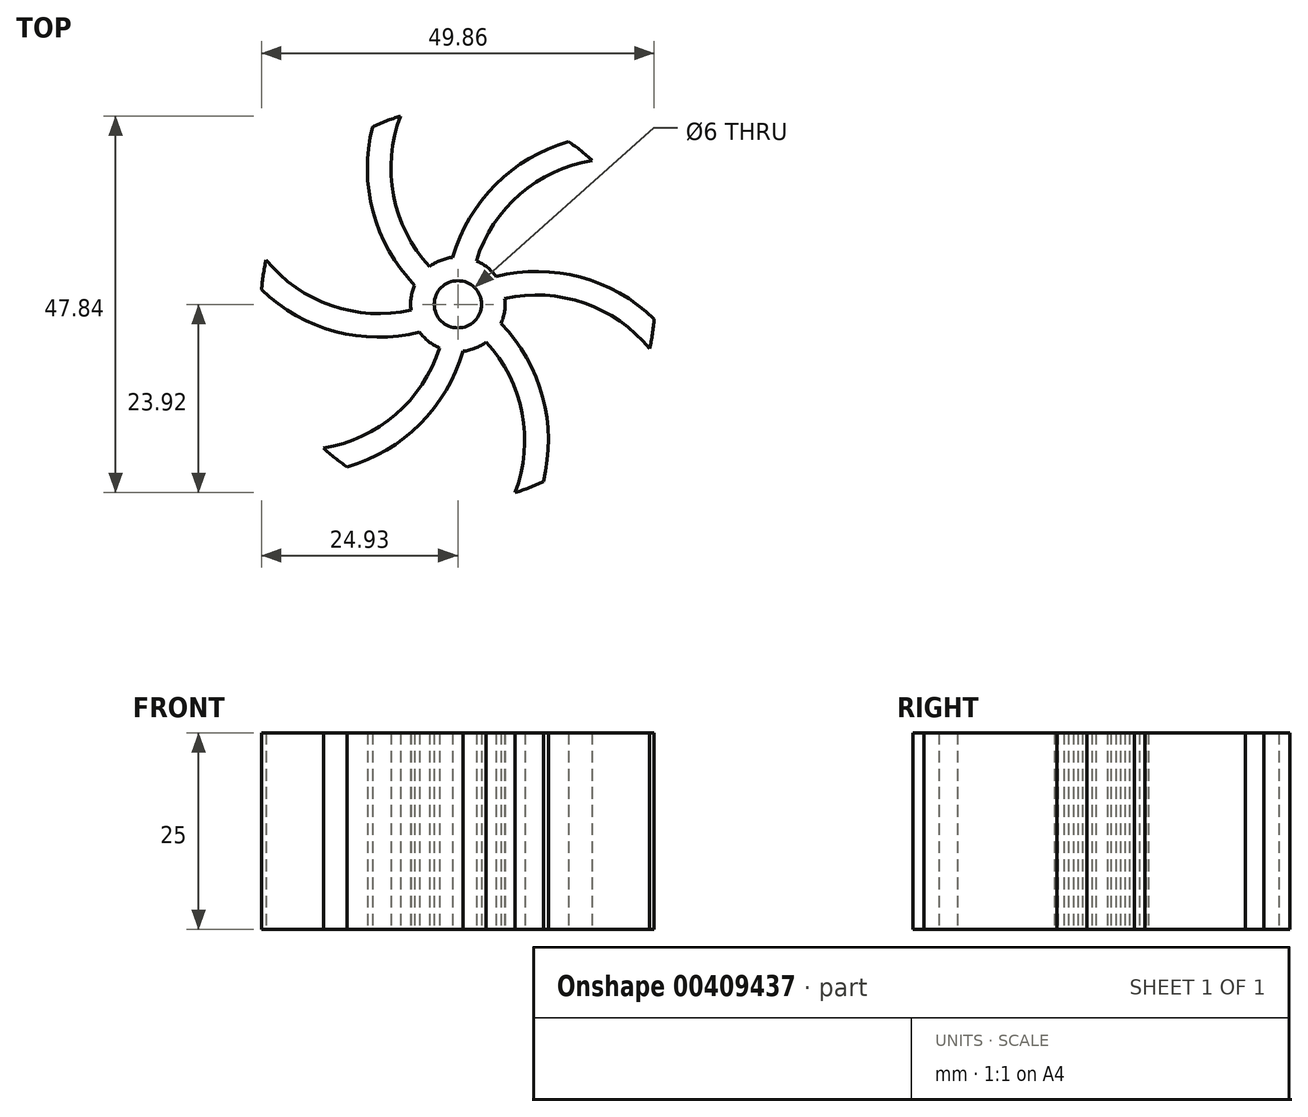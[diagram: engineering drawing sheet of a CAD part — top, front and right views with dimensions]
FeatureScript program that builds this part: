
annotation { "Feature Type Name" : "Feature", "Feature Type Description" : "" }
export const myFeature = defineFeature(function(context is Context, id is Id, definition is map)
    precondition{}
    {
        {
            var Q0;
            Q0=qCreatedBy(makeId("Top.planeOp"),FACE);
            var sketch = newSketch(context, id + "F0", { "sketchPlane" : qUnion([Q0])});
            skArc(sketch, "E0", {"start": v(17.07, 18.27) * mm, "mid": v(15.61, 19.52) * mm, "end": v(14.07, 20.67) * mm});
            skArc(sketch, "E1.0", {"start": v(14.07, 20.67) * mm, "mid": v(4.8, 15.21) * mm, "end": v(-0.66, 5.96) * mm});
            skArc(sketch, "E2.0", {"start": v(17.07, 18.27) * mm, "mid": v(7.9, 13.99) * mm, "end": v(2.34, 5.52) * mm});
            skArc(sketch, "E3.1.0", {"start": v(-7.28, 23.92) * mm, "mid": v(-8.17, 13.83) * mm, "end": v(-3.61, 4.8) * mm});
            skArc(sketch, "E3.1.1", {"start": v(-7.28, 23.92) * mm, "mid": v(-9.1, 23.28) * mm, "end": v(-10.86, 22.52) * mm});
            skArc(sketch, "E3.1.2", {"start": v(-10.86, 22.52) * mm, "mid": v(-10.77, 11.77) * mm, "end": v(-5.5, 2.41) * mm});
            skArc(sketch, "E3.2.0", {"start": v(-24.35, 5.65) * mm, "mid": v(-16.06, -0.16) * mm, "end": v(-5.96, -0.73) * mm});
            skArc(sketch, "E3.2.1", {"start": v(-24.35, 5.65) * mm, "mid": v(-24.72, 3.76) * mm, "end": v(-24.93, 1.85) * mm});
            skArc(sketch, "E3.2.2", {"start": v(-24.93, 1.85) * mm, "mid": v(-15.58, -3.44) * mm, "end": v(-4.84, -3.55) * mm});
            skArc(sketch, "E3.3.0", {"start": v(-17.07, -18.27) * mm, "mid": v(-7.9, -13.99) * mm, "end": v(-2.34, -5.52) * mm});
            skArc(sketch, "E3.3.1", {"start": v(-17.07, -18.27) * mm, "mid": v(-15.61, -19.52) * mm, "end": v(-14.07, -20.67) * mm});
            skArc(sketch, "E3.3.2", {"start": v(-14.07, -20.67) * mm, "mid": v(-4.8, -15.21) * mm, "end": v(0.66, -5.96) * mm});
            skArc(sketch, "E3.4.0", {"start": v(7.28, -23.92) * mm, "mid": v(8.17, -13.83) * mm, "end": v(3.61, -4.8) * mm});
            skArc(sketch, "E3.4.1", {"start": v(7.28, -23.92) * mm, "mid": v(9.1, -23.28) * mm, "end": v(10.86, -22.52) * mm});
            skArc(sketch, "E3.4.2", {"start": v(10.86, -22.52) * mm, "mid": v(10.77, -11.77) * mm, "end": v(5.5, -2.41) * mm});
            skArc(sketch, "E3.5.0", {"start": v(24.35, -5.65) * mm, "mid": v(16.06, 0.16) * mm, "end": v(5.96, 0.73) * mm});
            skArc(sketch, "E3.5.1", {"start": v(24.35, -5.65) * mm, "mid": v(24.72, -3.76) * mm, "end": v(24.93, -1.85) * mm});
            skArc(sketch, "E3.5.2", {"start": v(24.93, -1.85) * mm, "mid": v(15.58, 3.44) * mm, "end": v(4.84, 3.55) * mm});
            skArc(sketch, "E4", {"start": v(-5.5, 2.41) * mm, "mid": v(-5.94, 0.87) * mm, "end": v(-5.96, -0.73) * mm});
            skPoint(sketch, "E5.orphan", {"position": v(-1.5, 0) * mm});
            skPoint(sketch, "E6.orphan", {"position": v(-0.75, 1.3) * mm});
            skPoint(sketch, "E7.orphan", {"position": v(0.75, 1.3) * mm});
            skPoint(sketch, "E8.orphan", {"position": v(-0.75, -1.3) * mm});
            skPoint(sketch, "E9.orphan", {"position": v(0.75, -1.3) * mm});
            skArc(sketch, "E10.trimOffspring", {"start": v(-0.66, 5.96) * mm, "mid": v(-2.21, 5.58) * mm, "end": v(-3.61, 4.8) * mm});
            skArc(sketch, "E11.trimOffspring", {"start": v(4.84, 3.55) * mm, "mid": v(3.72, 4.7) * mm, "end": v(2.34, 5.52) * mm});
            skArc(sketch, "E12.trimOffspring", {"start": v(5.5, -2.41) * mm, "mid": v(5.94, -0.87) * mm, "end": v(5.96, 0.73) * mm});
            skArc(sketch, "E13.trimOffspring", {"start": v(0.66, -5.96) * mm, "mid": v(2.21, -5.58) * mm, "end": v(3.61, -4.8) * mm});
            skArc(sketch, "E14.trimOffspring", {"start": v(-4.84, -3.55) * mm, "mid": v(-3.72, -4.7) * mm, "end": v(-2.34, -5.52) * mm});
            skCircle(sketch, "E15", {"center": v(0, 0) * mm, "radius": 3 * mm});
            skSolve(sketch);
        }
        {
            var Q0;
            Q0 = qSketchRegion(id + "F0", true);
            extrude(context, id + "F1", {"entities" : qUnion([Q0]), "depth" : 25 * mm, "offsetDistance" : 25 * mm});
        }
    });
